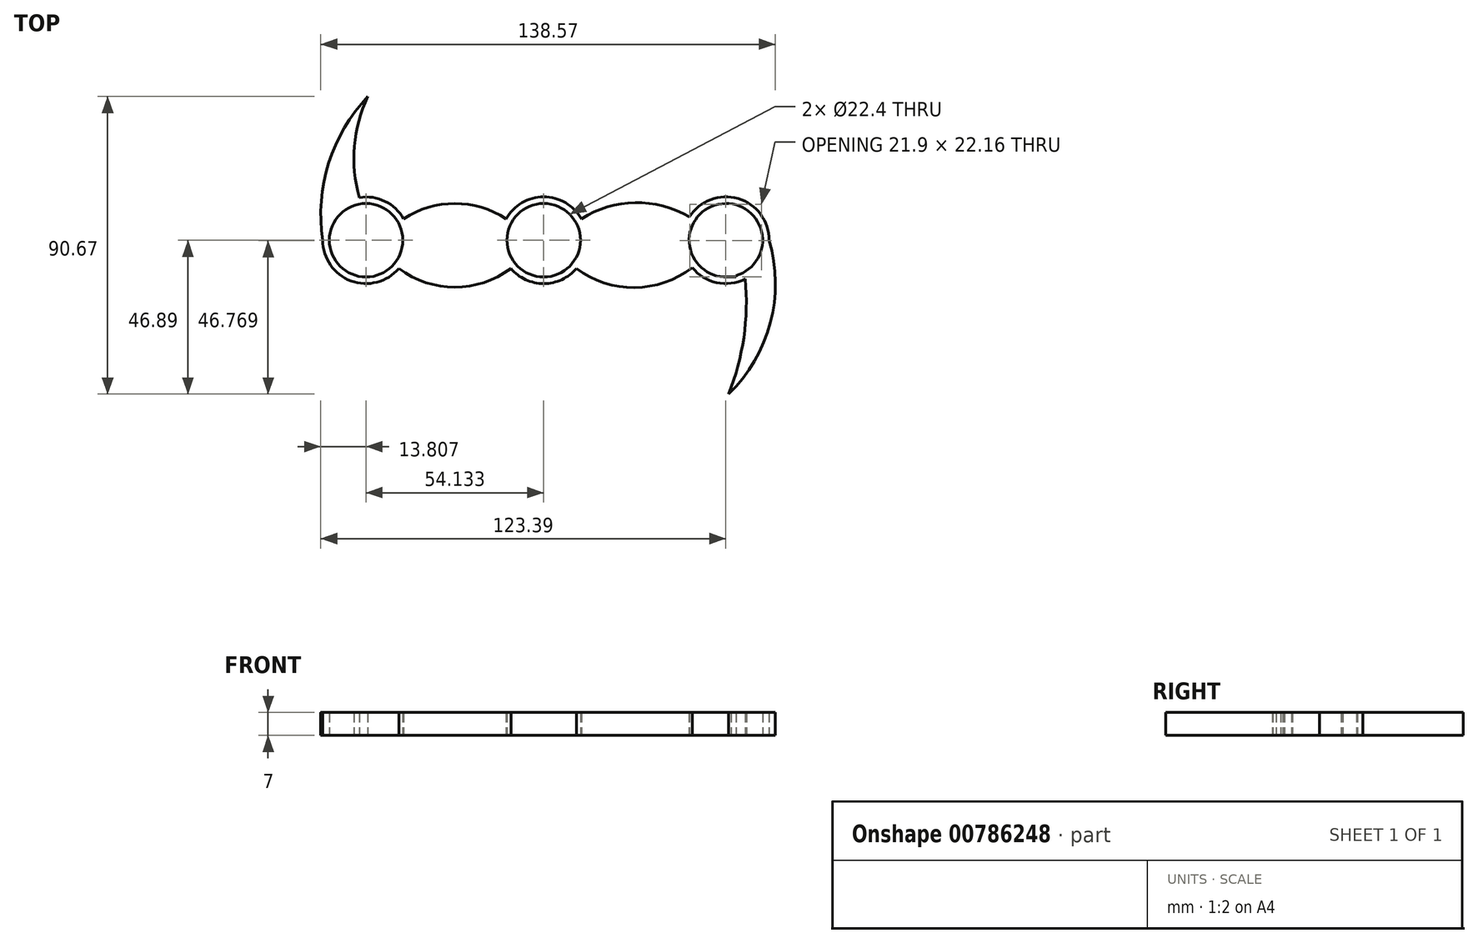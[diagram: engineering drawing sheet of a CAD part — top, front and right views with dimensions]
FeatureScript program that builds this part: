
annotation { "Feature Type Name" : "Feature", "Feature Type Description" : "" }
export const myFeature = defineFeature(function(context is Context, id is Id, definition is map)
    precondition{}
    {
        {
            var Q0;
            Q0=qCreatedBy(makeId("Top.planeOp"),FACE);
            var sketch = newSketch(context, id + "F0", { "sketchPlane" : qUnion([Q0])});
            skArc(sketch, "E0", {"start": v(11.48, 6.52) * mm, "mid": v(0, 13.2) * mm, "end": v(-11.48, 6.52) * mm});
            skArc(sketch, "E1", {"start": v(-42.65, 6.52) * mm, "mid": v(-67.27, 1.28) * mm, "end": v(-44.13, -8.6) * mm});
            skArc(sketch, "E2", {"start": v(54.41, -11.14) * mm, "mid": v(55.19, -11.04) * mm, "end": v(55.95, -10.88) * mm});
            skArc(sketch, "E3", {"start": v(57.07, 11.1) * mm, "mid": v(56.5, 11) * mm, "end": v(55.95, 10.88) * mm});
            skArc(sketch, "E4", {"start": v(57.07, 11.1) * mm, "mid": v(55.74, 11.2) * mm, "end": v(54.41, 11.14) * mm});
            skArc(sketch, "E5.trimOffspring", {"start": v(55.95, -10.88) * mm, "mid": v(58.7, -11.2) * mm, "end": v(61.42, -10.84) * mm});
            skArc(sketch, "E6.trimOffspring", {"start": v(55.95, 10.88) * mm, "mid": v(55.19, 11.04) * mm, "end": v(54.41, 11.14) * mm});
            skArc(sketch, "E7.trimOffspring", {"start": v(54.41, -11.14) * mm, "mid": v(55.74, -11.2) * mm, "end": v(57.07, -11.1) * mm});
            skArc(sketch, "E8", {"start": v(57.07, -11.1) * mm, "mid": v(57.85, -10.96) * mm, "end": v(58.6, -10.77) * mm});
            skArc(sketch, "E9", {"start": v(45.27, -8.3) * mm, "mid": v(68.71, 0.75) * mm, "end": v(44.4, 7.09) * mm});
            skArc(sketch, "E10", {"start": v(44.4, 7.09) * mm, "mid": v(27.86, 11.45) * mm, "end": v(11.48, 6.52) * mm});
            skArc(sketch, "E11", {"start": v(-11.48, 6.52) * mm, "mid": v(-27.07, 11.21) * mm, "end": v(-42.65, 6.52) * mm});
            skArc(sketch, "E12", {"start": v(-53.57, 43.78) * mm, "mid": v(-65.55, 23.5) * mm, "end": v(-67.33, 0) * mm});
            skArc(sketch, "E13", {"start": v(-53.57, 43.78) * mm, "mid": v(-57.71, 28.65) * mm, "end": v(-56.15, 13.04) * mm});
            skLineSegment(sketch, "E14", {"start": v(58.6, -10.77) * mm, "end": v(58.6, -12.84) * mm});
            skPoint(sketch, "E15.end.orphan", {"position": v(68.73, 0) * mm});
            skArc(sketch, "E16", {"start": v(56.36, -46.9) * mm, "mid": v(69.08, -25.17) * mm, "end": v(68.73, 0) * mm});
            skPoint(sketch, "E17.trimOffspring.end.orphan", {"position": v(58.6, -46.9) * mm});
            skPoint(sketch, "E18.end.orphan", {"position": v(0, -13.2) * mm});
            skArc(sketch, "E19", {"start": v(10, -8.6) * mm, "mid": v(27.69, -14.41) * mm, "end": v(45.27, -8.3) * mm});
            skArc(sketch, "E20", {"start": v(-44.13, -8.6) * mm, "mid": v(-27.07, -14.3) * mm, "end": v(-10, -8.6) * mm});
            skPoint(sketch, "E21.end.orphan", {"position": v(61.42, -11.81) * mm});
            skArc(sketch, "E22", {"start": v(56.36, -46.9) * mm, "mid": v(60.99, -29.65) * mm, "end": v(61.42, -11.81) * mm});
            skCircle(sketch, "E23", {"center": v(-54.13, 0) * mm, "radius": 11.2 * mm});
            skCircle(sketch, "E24", {"center": v(0, 0) * mm, "radius": 11.2 * mm});
            skArc(sketch, "E25.trimOffspring", {"start": v(-10, -8.6) * mm, "mid": v(0, -13.2) * mm, "end": v(10, -8.6) * mm});
            skCircle(sketch, "E26", {"center": v(55.53, 0) * mm, "radius": 11.2 * mm});
            skSolve(sketch);
        }
        {
            var Q0;
            Q0=makeQuery(id+"F0.imprint","IMPRINT",FACE,{"disambiguationData":[TD([[makeQuery(id+"F0.imprint","IMPRINT",EDGE,{"derivedFrom":sQuery(id+"F0.wireOp",EDGE,"E0")}),1.0]])]});
            var Q1;
            {var subQ0=sQuery(id+"F0.wireOp",EDGE,"E12");Q1=makeQuery(id+"F0.imprint","IMPRINT",FACE,{"disambiguationData":[TD([[makeQuery(id+"F0.imprint","IMPRINT",EDGE,{"derivedFrom":subQ0}),1.0]])]});}
            var Q2;
            {var subQ0=sQuery(id+"F0.wireOp",EDGE,"E16");Q2=makeQuery(id+"F0.imprint","IMPRINT",FACE,{"disambiguationData":[TD([[makeQuery(id+"F0.imprint","IMPRINT",EDGE,{"derivedFrom":subQ0}),1.0]])]});}
            extrude(context, id + "F1", {"entities" : qUnion([Q0, Q1, Q2]), "depth" : 7 * mm, "offsetDistance" : 25 * mm});
        }
    });
